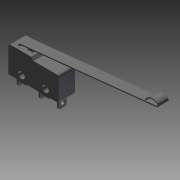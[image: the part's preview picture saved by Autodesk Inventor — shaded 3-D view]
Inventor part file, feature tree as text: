
AUTODESK INVENTOR PART (.ipt)
format: ipt  version: 2013 (Build 170138000, 138)  size: 178,688 bytes
history: native  units: mm (DEFAULTED — no unit token found)
features: imported_body x1, plane x1
ambient origin geometry x8: Origin, YZ Plane, XZ Plane, XY Plane, X Axis, Y Axis, Z Axis, Center Point
bodies: Solid1 (feature_tree)
feature tree (2):
  imported_body  "Base1"
  plane  "Work Plane1"
